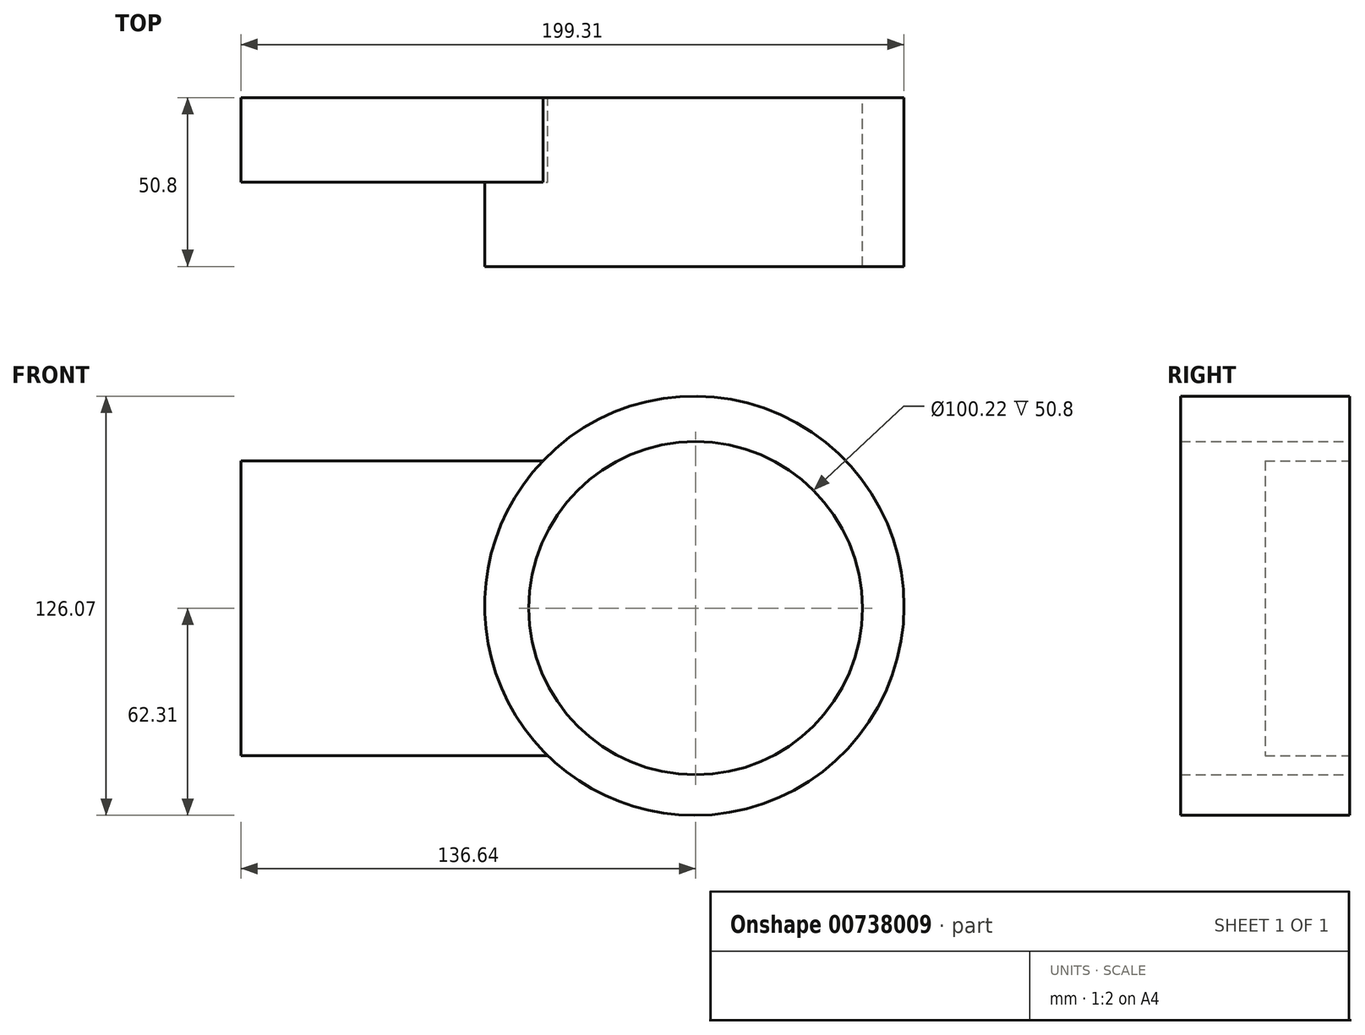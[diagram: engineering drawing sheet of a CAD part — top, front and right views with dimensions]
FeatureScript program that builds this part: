
annotation { "Feature Type Name" : "Feature", "Feature Type Description" : "" }
export const myFeature = defineFeature(function(context is Context, id is Id, definition is map)
    precondition{}
    {
        {
            var Q0;
            Q0=qCreatedBy(makeId("Front.planeOp"),FACE);
            var sketch = newSketch(context, id + "F0", { "sketchPlane" : qUnion([Q0])});
            skCircle(sketch, "E0", {"center": v(0, 0) * mm, "radius": 50.11 * mm});
            skCircle(sketch, "E1", {"center": v(-0.36, 0.72) * mm, "radius": 63.03 * mm});
            skSolve(sketch);
        }
        {
            var Q0;
            Q0=makeQuery(id+"F0.imprint","IMPRINT",FACE,{"disambiguationData":[TD([[makeQuery(id+"F0.imprint","IMPRINT",EDGE,{"derivedFrom":sQuery(id+"F0.wireOp",EDGE,"E0")}),-1.0]])]});
            extrude(context, id + "F1", {"entities" : qUnion([Q0]), "depth" : 25.4 * mm, "offsetDistance" : 25.4 * mm});
        }
        {
            var Q0;
            Q0=makeQuery(id+"F1.opExtrude","CAP_FACE",FACE,{"disambiguationData":[OSD([sQuery(id+"F0.wireOp",EDGE,"E0"),sQuery(id+"F0.wireOp",EDGE,"E1")])],"isStart":false});
            extrude(context, id + "F2", {"entities" : qUnion([Q0]), "operationType" : NewBodyOperationType.ADD, "depth" : 25.4 * mm, "offsetDistance" : 25.4 * mm});
        }
        {
            var Q0;
            Q0=qCreatedBy(makeId("Front.planeOp"),FACE);
            var sketch = newSketch(context, id + "F3", { "sketchPlane" : qUnion([Q0])});
            skLineSegment(sketch, "E2.bottom", {"start": v(-136.64, 44.33) * mm, "end": v(11.59, 44.33) * mm});
            skLineSegment(sketch, "E2.top", {"start": v(-136.64, -44.33) * mm, "end": v(11.59, -44.33) * mm});
            skLineSegment(sketch, "E2.left", {"start": v(-136.64, 44.33) * mm, "end": v(-136.64, -44.33) * mm});
            skLineSegment(sketch, "E2.right", {"start": v(11.59, 44.33) * mm, "end": v(11.59, -44.33) * mm});
            skPoint(sketch, "E2.middle", {"position": v(-62.53, 0) * mm});
            skSolve(sketch);
        }
        {
            var Q0;
            Q0 = qSketchRegion(id + "F3", true);
            extrude(context, id + "F4", {"entities" : qUnion([Q0]), "operationType" : NewBodyOperationType.ADD, "depth" : 25.4 * mm, "offsetDistance" : 25.4 * mm});
        }
        {
            var Q0;
            {var subQ0=sQuery(id+"F3.wireOp",EDGE,"E2.top");var subQ1=sQuery(id+"F0.wireOp",EDGE,"E0");var subQ2=sQuery(id+"F3.wireOp",EDGE,"E2.bottom");var subQ3=sQuery(id+"F3.wireOp",EDGE,"E2.right");Q0=makeQuery(id+"F4.boolean.opBoolean","SPLIT",FACE,{"disambiguationData":[TD([makeQuery(id+"F1.opExtrude","SWEPT_FACE",FACE,{"disambiguationData":[OSD([subQ1])]})])],"derivedFrom":makeQuery(id+"F4.opExtrude","CAP_FACE",FACE,{"disambiguationData":[OSD([subQ2,subQ0,sQuery(id+"F3.wireOp",EDGE,"E2.left"),subQ3])],"isStart":false})});}
            extrude(context, id + "F5", {"entities" : qUnion([Q0]), "operationType" : NewBodyOperationType.REMOVE, "oppositeDirection" : true, "depth" : 25.4 * mm, "offsetDistance" : 25.4 * mm});
        }
    });
